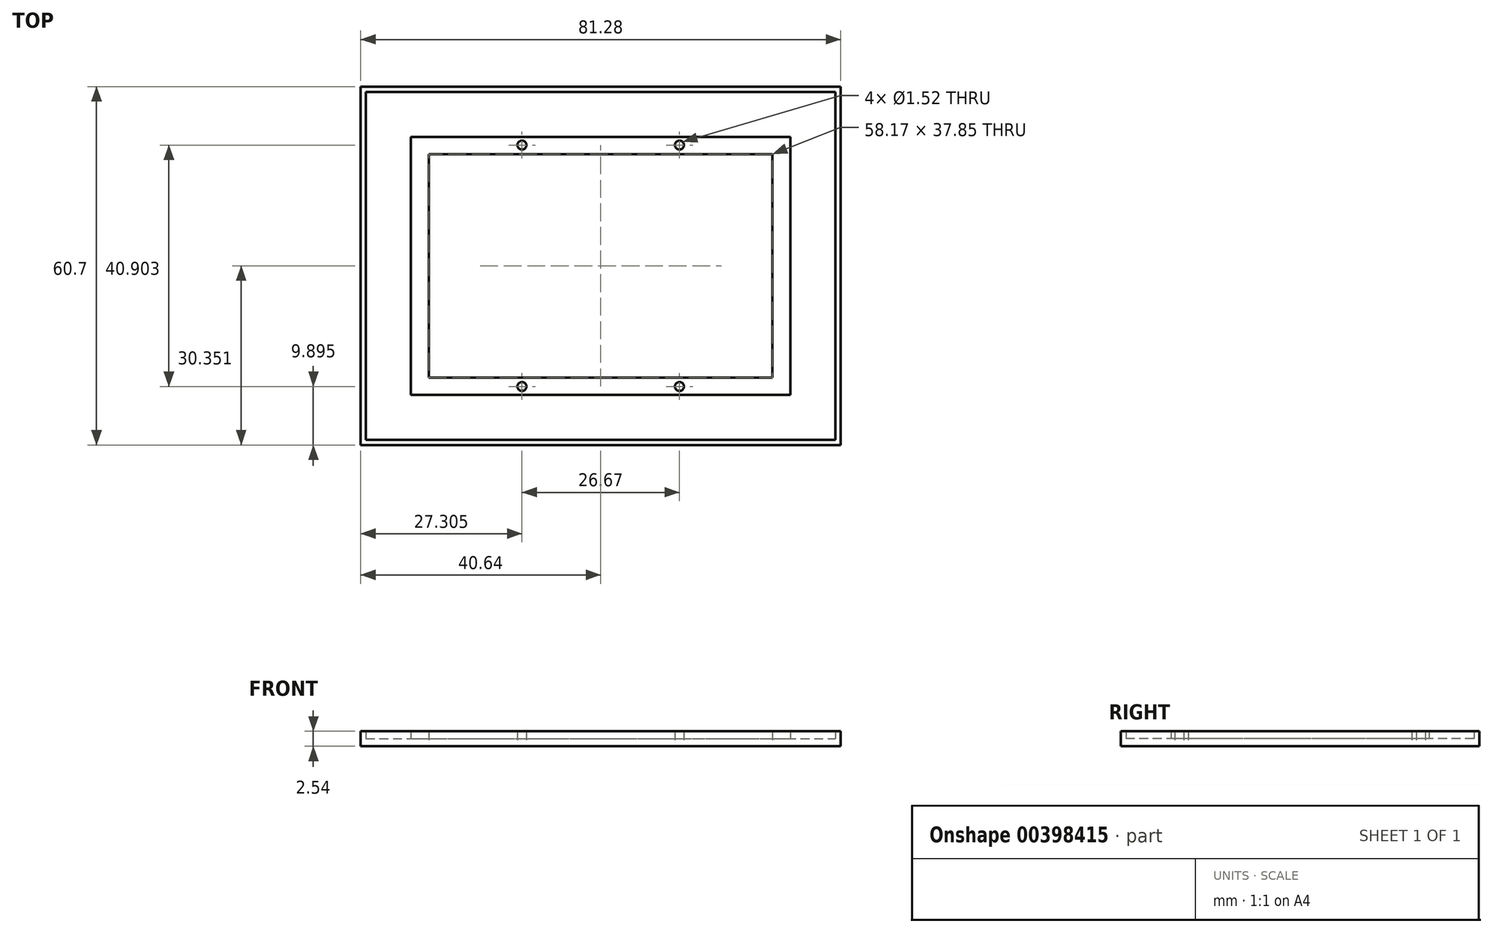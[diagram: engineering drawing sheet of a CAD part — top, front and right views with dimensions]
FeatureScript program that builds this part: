
annotation { "Feature Type Name" : "Feature", "Feature Type Description" : "" }
export const myFeature = defineFeature(function(context is Context, id is Id, definition is map)
    precondition{}
    {
        {
            var Q0;
            Q0=qCreatedBy(makeId("Top.planeOp"),FACE);
            var sketch = newSketch(context, id + "F0", { "sketchPlane" : qUnion([Q0])});
            skLineSegment(sketch, "E0.0", {"start": v(5.08, 0.88) * mm, "end": v(86.36, 0.88) * mm});
            skLineSegment(sketch, "E0.1", {"start": v(5.08, 0.88) * mm, "end": v(5.08, -59.82) * mm});
            skLineSegment(sketch, "E0.2", {"start": v(5.08, -59.82) * mm, "end": v(86.36, -59.82) * mm});
            skLineSegment(sketch, "E0.3", {"start": v(86.36, 0.88) * mm, "end": v(86.36, -59.82) * mm});
            skLineSegment(sketch, "E1", {"start": v(5.08, 0.88) * mm, "end": v(5.08, -29.47) * mm});
            skPoint(sketch, "E2.endSnap0", {"position": v(45.72, 0.88) * mm});
            skPoint(sketch, "E3.middle", {"position": v(45.72, -29.47) * mm});
            skLineSegment(sketch, "E4", {"start": v(45.72, -10.55) * mm, "end": v(74.8, -10.55) * mm});
            skLineSegment(sketch, "E5", {"start": v(74.8, -10.55) * mm, "end": v(74.8, -48.4) * mm});
            skLineSegment(sketch, "E6", {"start": v(74.8, -48.4) * mm, "end": v(45.72, -48.4) * mm});
            skLineSegment(sketch, "E7.MirrorCS", {"start": v(45.72, -10.55) * mm, "end": v(16.64, -10.55) * mm});
            skLineSegment(sketch, "E8.MirrorCS", {"start": v(16.64, -10.55) * mm, "end": v(16.64, -48.4) * mm});
            skLineSegment(sketch, "E9.MirrorCS", {"start": v(16.64, -48.4) * mm, "end": v(45.72, -48.4) * mm});
            skCircle(sketch, "E10", {"center": v(59.05, -9.02) * mm, "radius": 0.76 * mm});
            skCircle(sketch, "E11", {"center": v(32.39, -9.02) * mm, "radius": 0.76 * mm});
            skLineSegment(sketch, "E12", {"start": v(16.64, -48.4) * mm, "end": v(16.64, -49.93) * mm});
            skCircle(sketch, "E13", {"center": v(32.39, -49.93) * mm, "radius": 0.76 * mm});
            skCircle(sketch, "E14", {"center": v(59.05, -49.93) * mm, "radius": 0.76 * mm});
            skSolve(sketch);
        }
        {
            var Q0;
            Q0=makeQuery(id+"F0.imprint","IMPRINT",FACE,{"disambiguationData":[TD([[makeQuery(id+"F0.imprint","IMPRINT",EDGE,{"derivedFrom":sQuery(id+"F0.wireOp",EDGE,"E0.0")}),-1.0]])]});
            extrude(context, id + "F1", {"entities" : qUnion([Q0]), "depth" : 2.54 * mm});
        }
        {
            var Q0;
            Q0=qCreatedBy(makeId("Top.planeOp"),FACE);
            cPlane(context, id + "F2", {"entities" : qUnion([Q0]), "cplaneType" : CPlaneType.OFFSET, "offset" : 1.27 * mm, "width" : 152.4 * mm, "height" : 152.4 * mm});
        }
        {
            var Q0;
            Q0=qCreatedBy(id+"F2.planeOp",FACE);
            var sketch = newSketch(context, id + "F3", { "sketchPlane" : qUnion([Q0])});
            skLineSegment(sketch, "E15", {"start": v(0, 0) * mm, "end": v(5.97, 0) * mm});
            skLineSegment(sketch, "E16.bottom", {"start": v(5.97, 0) * mm, "end": v(85.47, 0) * mm});
            skLineSegment(sketch, "E16.top", {"start": v(5.97, -58.93) * mm, "end": v(85.47, -58.93) * mm});
            skLineSegment(sketch, "E16.left", {"start": v(5.97, 0) * mm, "end": v(5.97, -58.93) * mm});
            skLineSegment(sketch, "E16.right", {"start": v(85.47, 0) * mm, "end": v(85.47, -58.93) * mm});
            skLineSegment(sketch, "E17.0", {"start": v(13.59, -7.62) * mm, "end": v(77.85, -7.62) * mm});
            skLineSegment(sketch, "E17.1", {"start": v(13.59, -7.62) * mm, "end": v(13.59, -51.3) * mm});
            skLineSegment(sketch, "E17.2", {"start": v(13.59, -51.3) * mm, "end": v(77.85, -51.3) * mm});
            skLineSegment(sketch, "E17.3", {"start": v(77.85, -7.62) * mm, "end": v(77.85, -51.3) * mm});
            skSolve(sketch);
        }
        {
            var Q0;
            Q0 = qSketchRegion(id + "F3", true);
            extrude(context, id + "F4", {"entities" : qUnion([Q0]), "operationType" : NewBodyOperationType.REMOVE, "depth" : 1.27 * mm});
        }
    });
